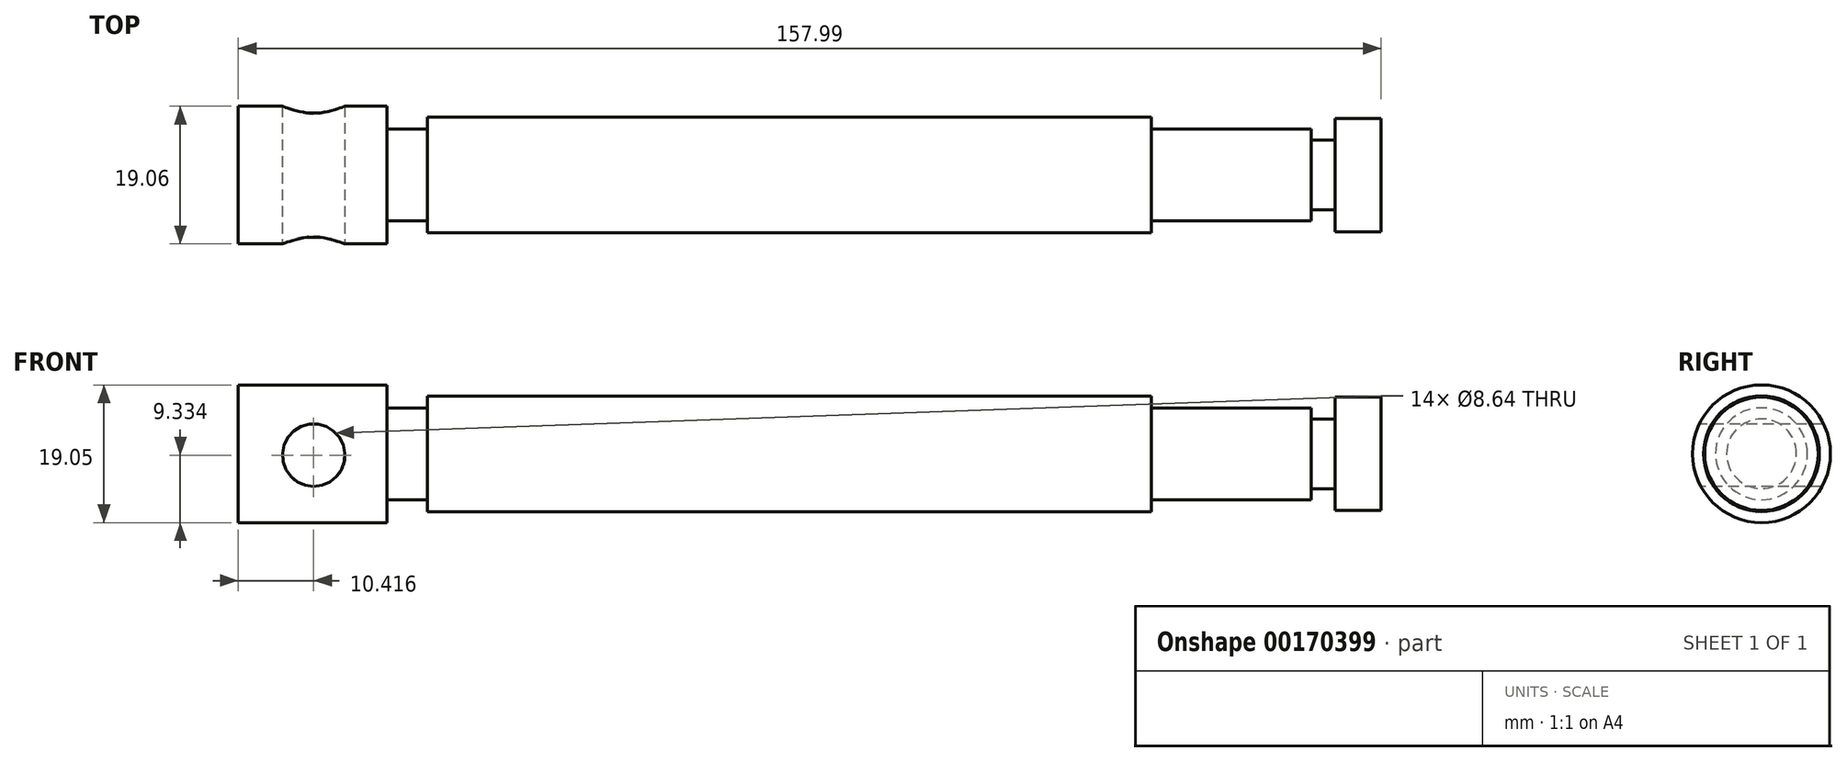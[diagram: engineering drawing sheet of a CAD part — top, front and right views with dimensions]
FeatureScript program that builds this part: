
annotation { "Feature Type Name" : "Feature", "Feature Type Description" : "" }
export const myFeature = defineFeature(function(context is Context, id is Id, definition is map)
    precondition{}
    {
        {
            var Q0;
            Q0=qCreatedBy(makeId("Front.planeOp"),FACE);
            var sketch = newSketch(context, id + "F0", { "sketchPlane" : qUnion([Q0])});
            skLineSegment(sketch, "E0", {"start": v(-75.96, 7.27) * mm, "end": v(82.03, 7.27) * mm});
            skLineSegment(sketch, "E1", {"start": v(-75.96, 7.27) * mm, "end": v(-75.96, 16.8) * mm});
            skLineSegment(sketch, "E2", {"start": v(-75.96, 16.8) * mm, "end": v(-55.38, 16.8) * mm});
            skLineSegment(sketch, "E3", {"start": v(-55.38, 16.8) * mm, "end": v(-55.38, 13.62) * mm});
            skLineSegment(sketch, "E4", {"start": v(-55.38, 13.62) * mm, "end": v(-49.82, 13.62) * mm});
            skLineSegment(sketch, "E5", {"start": v(-49.82, 13.62) * mm, "end": v(-49.82, 15.27) * mm});
            skLineSegment(sketch, "E6", {"start": v(-49.82, 15.27) * mm, "end": v(50.25, 15.27) * mm});
            skLineSegment(sketch, "E7", {"start": v(50.25, 15.27) * mm, "end": v(50.25, 13.62) * mm});
            skLineSegment(sketch, "E8", {"start": v(50.25, 13.62) * mm, "end": v(72.35, 13.62) * mm});
            skLineSegment(sketch, "E9", {"start": v(72.35, 13.62) * mm, "end": v(72.35, 12.1) * mm});
            skLineSegment(sketch, "E10", {"start": v(72.35, 12.1) * mm, "end": v(75.68, 12.1) * mm});
            skLineSegment(sketch, "E11", {"start": v(75.68, 12.1) * mm, "end": v(75.68, 15.12) * mm});
            skLineSegment(sketch, "E12", {"start": v(75.68, 15.12) * mm, "end": v(82.03, 15.12) * mm});
            skLineSegment(sketch, "E13", {"start": v(82.03, 15.12) * mm, "end": v(82.03, 7.27) * mm});
            skSolve(sketch);
        }
        {
            var Q0;
            Q0=makeQuery(id+"F0.imprint","IMPRINT",FACE,{"disambiguationData":[TD([[makeQuery(id+"F0.imprint","IMPRINT",EDGE,{"derivedFrom":sQuery(id+"F0.wireOp",EDGE,"E0")}),1.0]])]});
            var Q1;
            Q1=makeQuery(id+"F0.imprint","IMPRINT",FACE,{"disambiguationData":[TD([[makeQuery(id+"F0.imprint","IMPRINT",EDGE,{"derivedFrom":sQuery(id+"F0.wireOp",EDGE,"E0")}),1.0]])]});
            var Q2;
            Q2=sQuery(id+"F0.wireOp",EDGE,"E0");
            revolve(context, id + "F1", {"entities" : qUnion([Q0, Q1]), "axis" : qUnion([Q2]), "revolveType" : RevolveType.FULL});
        }
        {
            var Q0;
            Q0=qCreatedBy(makeId("Front.planeOp"),FACE);
            var sketch = newSketch(context, id + "F2", { "sketchPlane" : qUnion([Q0])});
            skCircle(sketch, "E14", {"center": v(-65.54, 7.08) * mm, "radius": 4.32 * mm});
            skLineSegment(sketch, "E15", {"start": v(-55.4, -2.44) * mm, "end": v(-75.99, -2.44) * mm, "construction": true});
            skSolve(sketch);
        }
        {
            var Q0;
            Q0 = qSketchRegion(id + "F2", true);
            extrude(context, id + "F3", {"entities" : qUnion([Q0]), "operationType" : NewBodyOperationType.REMOVE, "endBound" : BoundingType.SYMMETRIC, "oppositeDirection" : true, "depth" : 254 * mm});
        }
    });
